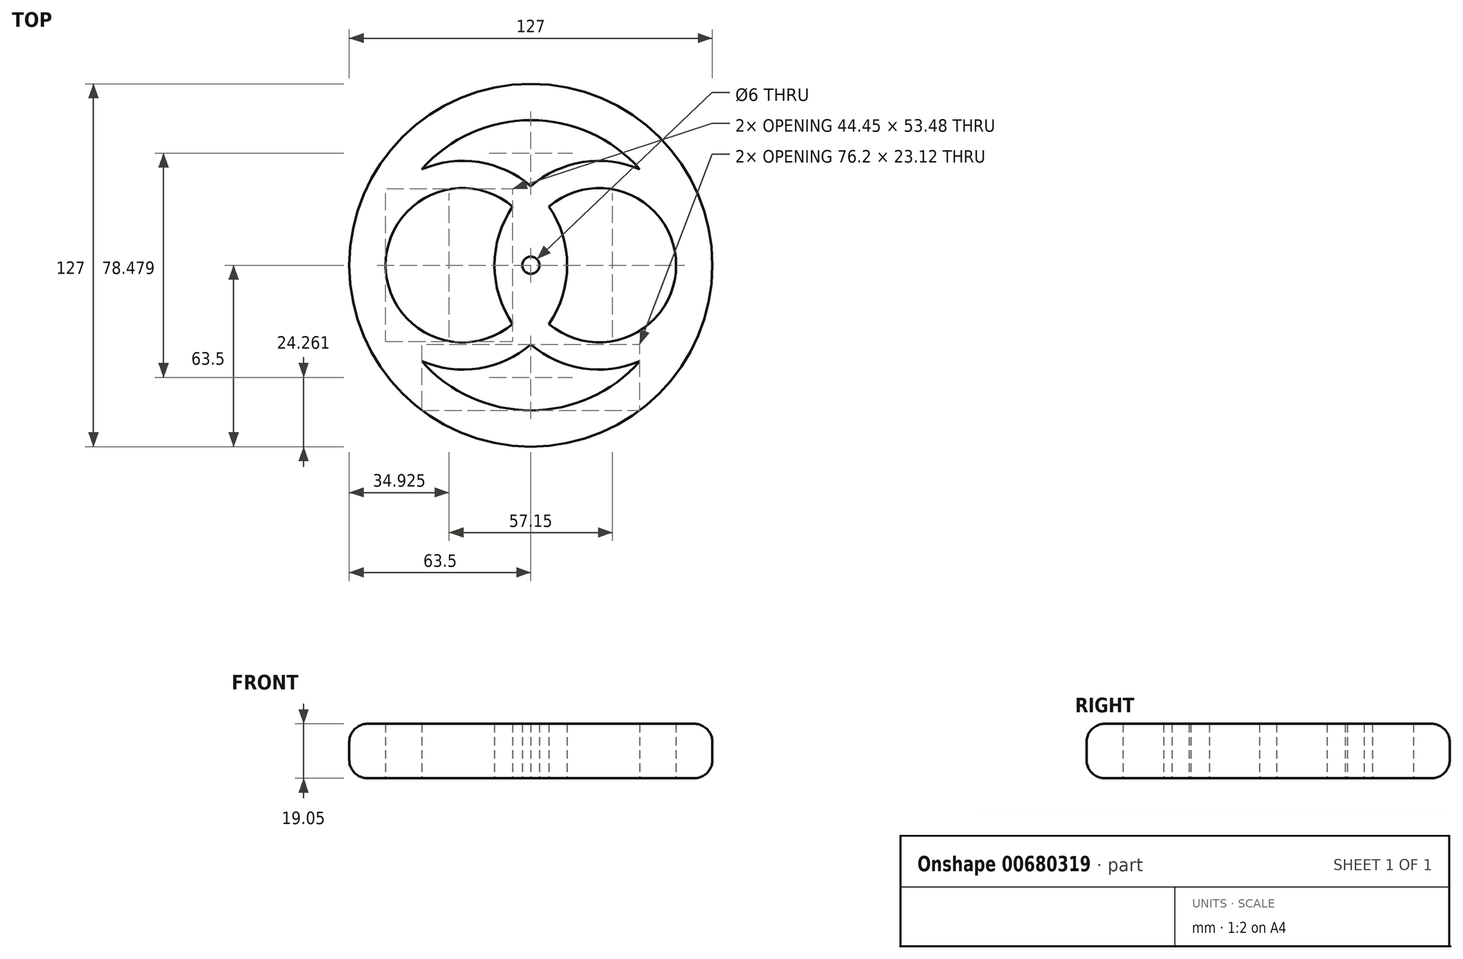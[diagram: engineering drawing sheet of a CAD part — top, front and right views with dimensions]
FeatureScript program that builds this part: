
annotation { "Feature Type Name" : "Feature", "Feature Type Description" : "" }
export const myFeature = defineFeature(function(context is Context, id is Id, definition is map)
    precondition{}
    {
        {
            var Q0;
            Q0=qCreatedBy(makeId("Top.planeOp"),FACE);
            var sketch = newSketch(context, id + "F0", { "sketchPlane" : qUnion([Q0])});
            skCircle(sketch, "E0", {"center": v(0, 0) * mm, "radius": 63.5 * mm});
            skCircle(sketch, "E1", {"center": v(0, 0) * mm, "radius": 12.7 * mm, "construction": true});
            skCircle(sketch, "E2", {"center": v(0, 0) * mm, "radius": 3 * mm});
            skArc(sketch, "E3", {"start": v(-38.1, -33.6) * mm, "mid": v(0, -50.8) * mm, "end": v(38.1, -33.6) * mm});
            skArc(sketch, "E4", {"start": v(-6.35, 20.58) * mm, "mid": v(-35.15, 24.5) * mm, "end": v(-50.8, 0) * mm});
            skArc(sketch, "E5", {"start": v(12.7, 0) * mm, "mid": v(11.08, 10.77) * mm, "end": v(6.35, 20.58) * mm});
            skArc(sketch, "E6.MirrorCS", {"start": v(-6.35, -20.58) * mm, "mid": v(-35.15, -24.5) * mm, "end": v(-50.8, 0) * mm});
            skArc(sketch, "E7.MirrorCS", {"start": v(12.7, 0) * mm, "mid": v(11.08, -10.77) * mm, "end": v(6.35, -20.58) * mm});
            skArc(sketch, "E8.MirrorCS", {"start": v(-12.7, 0) * mm, "mid": v(-11.08, 10.77) * mm, "end": v(-6.35, 20.58) * mm});
            skArc(sketch, "E9.MirrorCS", {"start": v(6.35, 20.58) * mm, "mid": v(35.15, 24.5) * mm, "end": v(50.8, 0) * mm});
            skArc(sketch, "E10.MirrorCS", {"start": v(6.35, -20.58) * mm, "mid": v(35.15, -24.5) * mm, "end": v(50.8, 0) * mm});
            skArc(sketch, "E11.MirrorCS", {"start": v(-12.7, 0) * mm, "mid": v(-11.08, -10.77) * mm, "end": v(-6.35, -20.58) * mm});
            skPoint(sketch, "E12.orphan", {"position": v(0, 12.7) * mm});
            skArc(sketch, "E13.trimOffspring", {"start": v(0, 27.68) * mm, "mid": v(-18.2, 36.08) * mm, "end": v(-38.1, 33.6) * mm});
            skArc(sketch, "E14.trimOffspring", {"start": v(0, 27.68) * mm, "mid": v(18.2, 36.08) * mm, "end": v(38.1, 33.6) * mm});
            skPoint(sketch, "E15.orphan", {"position": v(0, -12.7) * mm});
            skArc(sketch, "E16.trimOffspring", {"start": v(0, -27.68) * mm, "mid": v(18.2, -36.08) * mm, "end": v(38.1, -33.6) * mm});
            skArc(sketch, "E17.trimOffspring", {"start": v(0, -27.68) * mm, "mid": v(-18.2, -36.08) * mm, "end": v(-38.1, -33.6) * mm});
            skArc(sketch, "E18.trimOffspring", {"start": v(38.1, 33.6) * mm, "mid": v(0, 50.8) * mm, "end": v(-38.1, 33.6) * mm});
            skSolve(sketch);
        }
        {
            var Q0;
            Q0 = qSketchRegion(id + "F0", true);
            extrude(context, id + "F1", {"entities" : qUnion([Q0]), "depth" : 19.05 * mm, "offsetDistance" : 25.4 * mm});
        }
        {
            var Q0;
            Q0=makeQuery(id+"F1.opExtrude","SWEPT_FACE",FACE,{"disambiguationData":[OSD([sQuery(id+"F0.wireOp",EDGE,"E0")])]});
            fillet(context, id + "F2", {"entities" : qUnion([Q0]), "radius" : 6.35 * mm, "tangentPropagation" : true, "allowEdgeOverflow" : false});
        }
    });
